annotation { "Feature Type Name" : "Feature", "Feature Type Description" : "" }
export const myFeature = defineFeature(function(context is Context, id is Id, definition is map)
    precondition{}
    {
        {
            var Q0;
            Q0=qCreatedBy(makeId("Front.planeOp"),FACE);
            var sketch = newSketch(context, id + "F0", { "sketchPlane" : qUnion([Q0])});
            skLineSegment(sketch, "E0", {"start": v(0, 0) * mm, "end": v(-4572, 0) * mm});
            skLineSegment(sketch, "E1", {"start": v(0, 0) * mm, "end": v(4572, 0) * mm});
            skLineSegment(sketch, "E2", {"start": v(4572, 0) * mm, "end": v(4572, 3352.8) * mm});
            skLineSegment(sketch, "E3", {"start": v(-4572, 0) * mm, "end": v(-4572, 3352.8) * mm});
            skLineSegment(sketch, "E4", {"start": v(-4572, 3352.8) * mm, "end": v(4572, 3352.8) * mm});
            skLineSegment(sketch, "E5", {"start": v(4572, 0) * mm, "end": v(9144, 0) * mm});
            skLineSegment(sketch, "E6", {"start": v(9144, 0) * mm, "end": v(9144, -609.6) * mm});
            skLineSegment(sketch, "E7", {"start": v(9144, -609.6) * mm, "end": v(-4572, -609.6) * mm});
            skLineSegment(sketch, "E8", {"start": v(-4572, -609.6) * mm, "end": v(-4572, 0) * mm});
            skLineSegment(sketch, "E9", {"start": v(0, 3352.8) * mm, "end": v(0, 5638.8) * mm});
            skLineSegment(sketch, "E10", {"start": v(-4572, 3352.8) * mm, "end": v(0, 5638.8) * mm});
            skLineSegment(sketch, "E11", {"start": v(4572, 3352.8) * mm, "end": v(0, 5638.8) * mm});
            skLineSegment(sketch, "E12", {"start": v(0, 5638.8) * mm, "end": v(0, 6096) * mm});
            skLineSegment(sketch, "E13", {"start": v(-4572, 3352.8) * mm, "end": v(-5486.4, 3352.8) * mm});
            skLineSegment(sketch, "E14", {"start": v(0, 6096) * mm, "end": v(-5486.4, 3352.8) * mm});
            skLineSegment(sketch, "E15", {"start": v(4572, 3352.8) * mm, "end": v(5486.4, 3352.8) * mm});
            skLineSegment(sketch, "E16", {"start": v(5486.4, 3352.8) * mm, "end": v(0, 6096) * mm});
            skLineSegment(sketch, "E17", {"start": v(9144, 0) * mm, "end": v(9144, 2743.2) * mm});
            skLineSegment(sketch, "E18", {"start": v(9144, 2743.2) * mm, "end": v(4572, 3352.8) * mm});
            skLineSegment(sketch, "E19", {"start": v(4572, 2743.2) * mm, "end": v(9144, 2133.6) * mm});
            skLineSegment(sketch, "E20", {"start": v(-3352.8, 0) * mm, "end": v(-3352.8, 2133.6) * mm});
            skLineSegment(sketch, "E21", {"start": v(-3352.8, 2133.6) * mm, "end": v(-2438.4, 2133.6) * mm});
            skLineSegment(sketch, "E22", {"start": v(-2438.4, 2133.6) * mm, "end": v(-2438.4, 0) * mm});
            skLineSegment(sketch, "E23", {"start": v(-2438.4, 0) * mm, "end": v(-2133.6, 0) * mm});
            skLineSegment(sketch, "E24", {"start": v(-2133.6, 0) * mm, "end": v(-2133.6, 2438.4) * mm});
            skLineSegment(sketch, "E25", {"start": v(-3352.8, 0) * mm, "end": v(-3657.6, 0) * mm});
            skLineSegment(sketch, "E26", {"start": v(-3657.6, 0) * mm, "end": v(-3657.6, 2438.8) * mm});
            skLineSegment(sketch, "E27", {"start": v(-3657.6, 2438.8) * mm, "end": v(-2133.6, 2438.4) * mm});
            skLineSegment(sketch, "E28.bottom", {"start": v(304.8, 2133.6) * mm, "end": v(3048, 2133.6) * mm});
            skLineSegment(sketch, "E28.top", {"start": v(304.8, 762) * mm, "end": v(3048, 762) * mm});
            skLineSegment(sketch, "E28.left", {"start": v(304.8, 2133.6) * mm, "end": v(304.8, 762) * mm});
            skLineSegment(sketch, "E28.right", {"start": v(3048, 2133.6) * mm, "end": v(3048, 762) * mm});
            skLineSegment(sketch, "E29.0", {"start": v(457.2, 1981.2) * mm, "end": v(457.2, 914.4) * mm});
            skLineSegment(sketch, "E29.1", {"start": v(457.2, 1981.2) * mm, "end": v(2895.6, 1981.2) * mm});
            skLineSegment(sketch, "E29.2", {"start": v(2895.6, 1981.2) * mm, "end": v(2895.6, 914.4) * mm});
            skLineSegment(sketch, "E29.3", {"start": v(457.2, 914.4) * mm, "end": v(2895.6, 914.4) * mm});
            skLineSegment(sketch, "E30.bottom", {"start": v(7315.2, 762) * mm, "end": v(6096, 762) * mm});
            skLineSegment(sketch, "E30.top", {"start": v(7315.2, 1981.2) * mm, "end": v(6096, 1981.2) * mm});
            skLineSegment(sketch, "E30.left", {"start": v(7315.2, 762) * mm, "end": v(7315.2, 1981.2) * mm});
            skLineSegment(sketch, "E30.right", {"start": v(6096, 762) * mm, "end": v(6096, 1981.2) * mm});
            skLineSegment(sketch, "E31.bottom", {"start": v(6248.4, 1828.8) * mm, "end": v(7162.8, 1828.8) * mm});
            skLineSegment(sketch, "E31.top", {"start": v(6248.4, 914.4) * mm, "end": v(7162.8, 914.4) * mm});
            skLineSegment(sketch, "E31.left", {"start": v(6248.4, 1828.8) * mm, "end": v(6248.4, 914.4) * mm});
            skLineSegment(sketch, "E31.right", {"start": v(7162.8, 1828.8) * mm, "end": v(7162.8, 914.4) * mm});
            skText(sketch, "E32", { "text": "Ethan Porter", "fontName": "OpenSans-Regular.ttf"});
            const initialGuessF0  = {"E32": [-6.13754, -3.06182, 1, 0, 1.85038]};
            skSetInitialGuess(sketch, initialGuessF0);
            skSolve(sketch);
        }
        {
            var Q0;
            Q0=makeQuery(id+"F0.imprint","IMPRINT",FACE,{"disambiguationData":[TD([[makeQuery(id+"F0.imprint","IMPRINT",EDGE,{"derivedFrom":sQuery(id+"F0.wireOp",EDGE,"E10")}),1.0]])]});
            var Q1;
            Q1=makeQuery(id+"F0.imprint","IMPRINT",FACE,{"disambiguationData":[TD([[makeQuery(id+"F0.imprint","IMPRINT",EDGE,{"derivedFrom":sQuery(id+"F0.wireOp",EDGE,"E11")}),-1.0]])]});
            extrude(context, id + "F1", {"entities" : qUnion([Q0, Q1]), "depth" : 914.4 * mm, "offsetDistance" : 30.48 * mm, "hasSecondDirection" : true, "secondDirectionOppositeDirection" : true, "secondDirectionDepth" : 12192 * mm});
        }
        {
            var Q0;
            {var subQ2=sQuery(id+"F0.wireOp",EDGE,"E9");Q0=makeQuery(id+"F0.imprint","IMPRINT",FACE,{"disambiguationData":[TD([[makeQuery(id+"F0.imprint","IMPRINT",EDGE,{"derivedFrom":subQ2}),1.0]])]});}
            var Q1;
            {var subQ2=sQuery(id+"F0.wireOp",EDGE,"E9");Q1=makeQuery(id+"F0.imprint","IMPRINT",FACE,{"disambiguationData":[TD([[makeQuery(id+"F0.imprint","IMPRINT",EDGE,{"derivedFrom":subQ2}),-1.0]])]});}
            extrude(context, id + "F2", {"entities" : qUnion([Q0, Q1]), "operationType" : NewBodyOperationType.ADD, "depth" : 609.6 * mm, "offsetDistance" : 30.48 * mm, "hasSecondDirection" : true, "secondDirectionOppositeDirection" : true, "secondDirectionDepth" : 12192 * mm});
        }
        {
            var Q0;
            Q0=makeQuery(id+"F0.imprint","IMPRINT",FACE,{"disambiguationData":[TD([[makeQuery(id+"F0.imprint","IMPRINT",EDGE,{"derivedFrom":sQuery(id+"F0.wireOp",EDGE,"E29.0")}),1.0]])]});
            var Q1;
            Q1=makeQuery(id+"F0.imprint","IMPRINT",FACE,{"disambiguationData":[TD([[makeQuery(id+"F0.imprint","IMPRINT",EDGE,{"derivedFrom":sQuery(id+"F0.wireOp",EDGE,"E31.bottom")}),-1.0]])]});
            extrude(context, id + "F3", {"entities" : qUnion([Q0, Q1]), "depth" : 304.8 * mm, "offsetDistance" : 30.48 * mm, "hasSecondDirection" : true, "secondDirectionOppositeDirection" : true, "secondDirectionDepth" : 12192 * mm});
        }
        {
            var Q0;
            Q0=makeQuery(id+"F3.opExtrude","CAP_FACE",FACE,{"disambiguationData":[OSD([sQuery(id+"F0.wireOp",EDGE,"E31.bottom"),sQuery(id+"F0.wireOp",EDGE,"E31.top"),sQuery(id+"F0.wireOp",EDGE,"E31.left"),sQuery(id+"F0.wireOp",EDGE,"E31.right")])],"isStart":false});
            var Q1;
            Q1=makeQuery(id+"F0.imprint","IMPRINT",FACE,{"disambiguationData":[TD([[makeQuery(id+"F0.imprint","IMPRINT",EDGE,{"derivedFrom":sQuery(id+"F0.wireOp",EDGE,"E28.bottom")}),-1.0]])]});
            var Q2;
            Q2=makeQuery(id+"F0.imprint","IMPRINT",FACE,{"disambiguationData":[TD([[makeQuery(id+"F0.imprint","IMPRINT",EDGE,{"derivedFrom":sQuery(id+"F0.wireOp",EDGE,"E30.bottom")}),-1.0]])]});
            extrude(context, id + "F4", {"entities" : qUnion([Q0, Q1, Q2]), "depth" : 487.68 * mm, "offsetDistance" : 30.48 * mm, "hasSecondDirection" : true, "secondDirectionOppositeDirection" : true, "secondDirectionDepth" : 12192 * mm});
        }
        {
            var Q0;
            {var subQ0=sQuery(id+"F0.wireOp",EDGE,"E20");Q0=makeQuery(id+"F0.imprint","IMPRINT",FACE,{"disambiguationData":[TD([[makeQuery(id+"F0.imprint","IMPRINT",EDGE,{"derivedFrom":subQ0}),-1.0]])]});}
            extrude(context, id + "F5", {"entities" : qUnion([Q0]), "depth" : 457.2 * mm, "offsetDistance" : 30.48 * mm, "hasSecondDirection" : true, "secondDirectionOppositeDirection" : true, "secondDirectionDepth" : 12192 * mm});
        }
        {
            var Q0;
            Q0=makeQuery(id+"F0.imprint","IMPRINT",FACE,{"disambiguationData":[TD([[makeQuery(id+"F0.imprint","IMPRINT",EDGE,{"derivedFrom":sQuery(id+"F0.wireOp",EDGE,"E20")}),1.0]])]});
            extrude(context, id + "F6", {"entities" : qUnion([Q0]), "operationType" : NewBodyOperationType.ADD, "depth" : 457.2 * mm, "offsetDistance" : 30.48 * mm, "hasSecondDirection" : true, "secondDirectionOppositeDirection" : true, "secondDirectionDepth" : 12192 * mm});
        }
        {
            var Q0;
            {var subQ8=sQuery(id+"F0.wireOp",EDGE,"E1");Q0=makeQuery(id+"F0.imprint","IMPRINT",FACE,{"disambiguationData":[TD([[makeQuery(id+"F0.imprint","IMPRINT",EDGE,{"derivedFrom":subQ8}),1.0]])]});}
            extrude(context, id + "F7", {"entities" : qUnion([Q0]), "depth" : 30.48 * mm, "offsetDistance" : 30.48 * mm, "hasSecondDirection" : true, "secondDirectionOppositeDirection" : true, "secondDirectionDepth" : 12192 * mm});
        }
        {
            var Q0;
            {var subQ0=sQuery(id+"F0.wireOp",EDGE,"E1");Q0=makeQuery(id+"F0.imprint","IMPRINT",FACE,{"disambiguationData":[TD([[makeQuery(id+"F0.imprint","IMPRINT",EDGE,{"derivedFrom":subQ0}),-1.0]])]});}
            extrude(context, id + "F8", {"entities" : qUnion([Q0]), "depth" : 1524 * mm, "offsetDistance" : 30.48 * mm, "hasSecondDirection" : true, "secondDirectionOppositeDirection" : true, "secondDirectionDepth" : 12192 * mm});
        }
        {
            var Q0;
            {var subQ1=sQuery(id+"F0.wireOp",EDGE,"E5");Q0=makeQuery(id+"F0.imprint","IMPRINT",FACE,{"disambiguationData":[TD([[makeQuery(id+"F0.imprint","IMPRINT",EDGE,{"derivedFrom":subQ1}),1.0]])]});}
            extrude(context, id + "F9", {"entities" : qUnion([Q0]), "depth" : 304.8 * mm, "offsetDistance" : 30.48 * mm, "hasSecondDirection" : true, "secondDirectionOppositeDirection" : true, "secondDirectionDepth" : 12192 * mm});
        }
        {
            var Q0;
            {var subQ0=sQuery(id+"F0.wireOp",EDGE,"E18");Q0=makeQuery(id+"F0.imprint","IMPRINT",FACE,{"disambiguationData":[TD([[makeQuery(id+"F0.imprint","IMPRINT",EDGE,{"derivedFrom":subQ0}),1.0]])]});}
            extrude(context, id + "F10", {"entities" : qUnion([Q0]), "depth" : 304.8 * mm, "offsetDistance" : 30.48 * mm, "hasSecondDirection" : true, "secondDirectionOppositeDirection" : true, "secondDirectionDepth" : 12192 * mm});
        }
        {
            var Q0;
            Q0=makeQuery(id+"F7.opExtrude","SWEPT_FACE",FACE,{"disambiguationData":[OSD([sQuery(id+"F0.wireOp",EDGE,"E3")])]});
            var sketch = newSketch(context, id + "F11", { "sketchPlane" : qUnion([Q0])});
            skLineSegment(sketch, "E33.bottom", {"start": v(-10628.73, 2382.6) * mm, "end": v(-9104.73, 2382.6) * mm});
            skLineSegment(sketch, "E33.top", {"start": v(-10628.73, 1468.2) * mm, "end": v(-9104.73, 1468.2) * mm});
            skLineSegment(sketch, "E33.left", {"start": v(-10628.73, 2382.6) * mm, "end": v(-10628.73, 1468.2) * mm});
            skLineSegment(sketch, "E33.right", {"start": v(-9104.73, 2382.6) * mm, "end": v(-9104.73, 1468.2) * mm});
            skLineSegment(sketch, "E34.0", {"start": v(-10781.13, 2535) * mm, "end": v(-8952.33, 2535) * mm});
            skLineSegment(sketch, "E34.1", {"start": v(-10781.13, 2535) * mm, "end": v(-10781.13, 1315.8) * mm});
            skLineSegment(sketch, "E34.2", {"start": v(-10781.13, 1315.8) * mm, "end": v(-8952.33, 1315.8) * mm});
            skLineSegment(sketch, "E34.3", {"start": v(-8952.33, 2535) * mm, "end": v(-8952.33, 1315.8) * mm});
            skLineSegment(sketch, "E35.bottom", {"start": v(-6294.6, 2501.3) * mm, "end": v(-4899.01, 2501.3) * mm});
            skLineSegment(sketch, "E35.top", {"start": v(-6294.6, 1540.69) * mm, "end": v(-4899.01, 1540.69) * mm});
            skLineSegment(sketch, "E35.left", {"start": v(-6294.6, 2501.3) * mm, "end": v(-6294.6, 1540.69) * mm});
            skLineSegment(sketch, "E35.right", {"start": v(-4899.01, 2501.3) * mm, "end": v(-4899.01, 1540.69) * mm});
            skLineSegment(sketch, "E36.0", {"start": v(-6507.96, 2714.65) * mm, "end": v(-6507.96, 1327.33) * mm});
            skLineSegment(sketch, "E36.1", {"start": v(-6507.96, 2714.65) * mm, "end": v(-4685.65, 2714.65) * mm});
            skLineSegment(sketch, "E36.2", {"start": v(-4685.65, 2714.65) * mm, "end": v(-4685.65, 1327.33) * mm});
            skLineSegment(sketch, "E36.3", {"start": v(-6507.96, 1327.33) * mm, "end": v(-4685.65, 1327.33) * mm});
            skSolve(sketch);
        }
        {
            var Q0;
            Q0=makeQuery(id+"F11.imprint","IMPRINT",FACE,{"disambiguationData":[TD([[makeQuery(id+"F11.imprint","IMPRINT",EDGE,{"derivedFrom":sQuery(id+"F11.wireOp",EDGE,"E33.bottom")}),1.0]])]});
            var Q1;
            Q1=makeQuery(id+"F11.imprint","IMPRINT",FACE,{"disambiguationData":[TD([[makeQuery(id+"F11.imprint","IMPRINT",EDGE,{"derivedFrom":sQuery(id+"F11.wireOp",EDGE,"E35.bottom")}),1.0]])]});
            extrude(context, id + "F12", {"entities" : qUnion([Q0, Q1]), "operationType" : NewBodyOperationType.ADD, "depth" : 304.8 * mm, "offsetDistance" : 30.48 * mm, "hasSecondDirection" : true, "secondDirectionOppositeDirection" : true, "secondDirectionDepth" : 12192 * mm});
        }
        {
            var Q0;
            Q0=makeQuery(id+"F11.imprint","IMPRINT",FACE,{"disambiguationData":[TD([[makeQuery(id+"F11.imprint","IMPRINT",EDGE,{"derivedFrom":sQuery(id+"F11.wireOp",EDGE,"E33.bottom")}),1.0]])]});
            var Q1;
            Q1=makeQuery(id+"F11.imprint","IMPRINT",FACE,{"disambiguationData":[TD([[makeQuery(id+"F11.imprint","IMPRINT",EDGE,{"derivedFrom":sQuery(id+"F11.wireOp",EDGE,"E35.bottom")}),1.0]])]});
            extrude(context, id + "F13", {"entities" : qUnion([Q0, Q1]), "depth" : 487.68 * mm, "offsetDistance" : 30.48 * mm, "hasSecondDirection" : true, "secondDirectionOppositeDirection" : true, "secondDirectionDepth" : 12192 * mm});
        }
    });